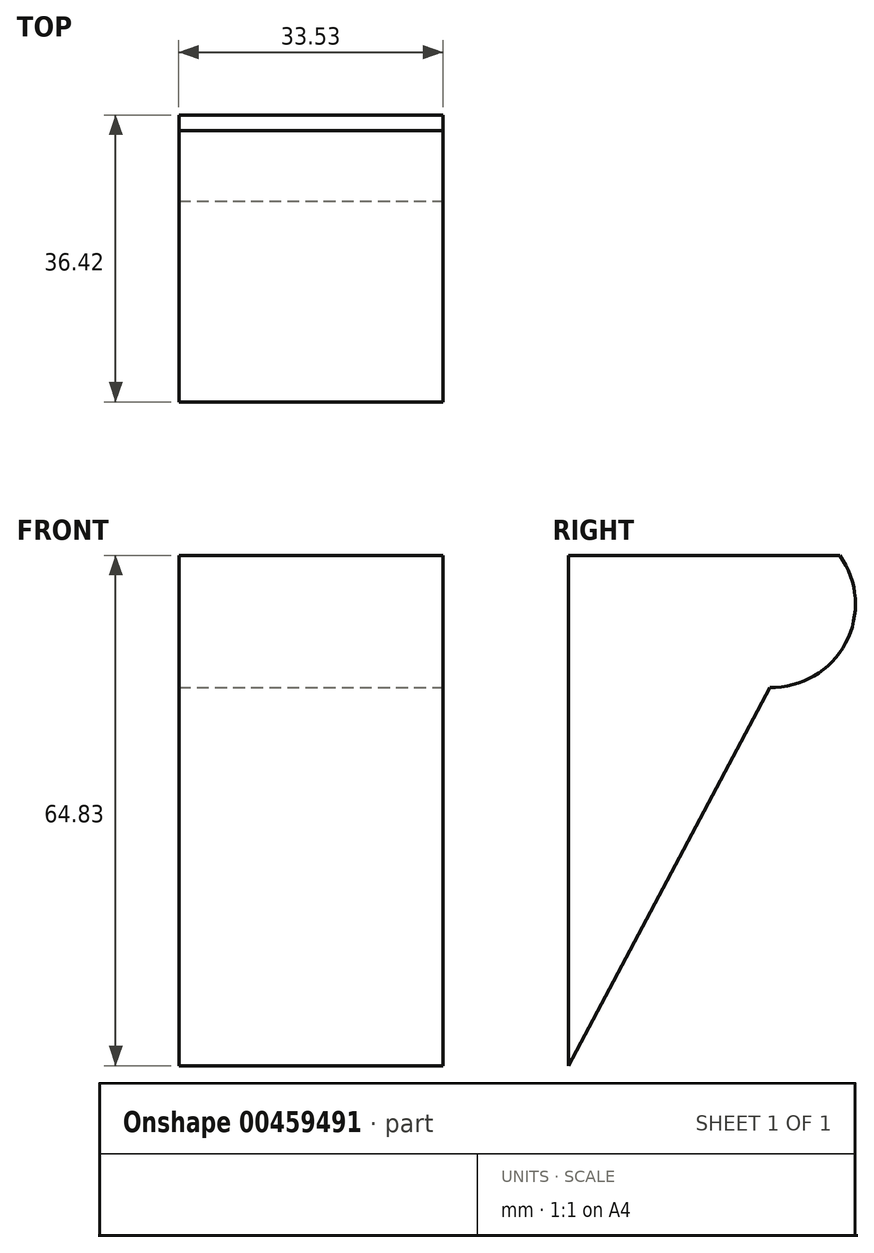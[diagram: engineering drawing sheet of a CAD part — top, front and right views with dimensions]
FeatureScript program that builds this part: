
annotation { "Feature Type Name" : "Feature", "Feature Type Description" : "" }
export const myFeature = defineFeature(function(context is Context, id is Id, definition is map)
    precondition{}
    {
        {
            var Q0;
            Q0=qCreatedBy(makeId("Right.planeOp"),FACE);
            var sketch = newSketch(context, id + "F0", { "sketchPlane" : qUnion([Q0])});
            skLineSegment(sketch, "E0", {"start": v(0, 0) * mm, "end": v(34.43, 0) * mm});
            skLineSegment(sketch, "E1", {"start": v(34.43, 0) * mm, "end": v(0, -64.83) * mm});
            skLineSegment(sketch, "E2", {"start": v(0, -64.83) * mm, "end": v(0, 0) * mm});
            skArc(sketch, "E3", {"start": v(17.22, 0) * mm, "mid": v(25.83, -16.77) * mm, "end": v(34.43, 0) * mm});
            skSolve(sketch);
        }
        {
            var Q0;
            Q0 = qSketchRegion(id + "F0", true);
            extrude(context, id + "F1", {"entities" : qUnion([Q0]), "oppositeDirection" : true, "depth" : 33.53 * mm});
        }
    });
